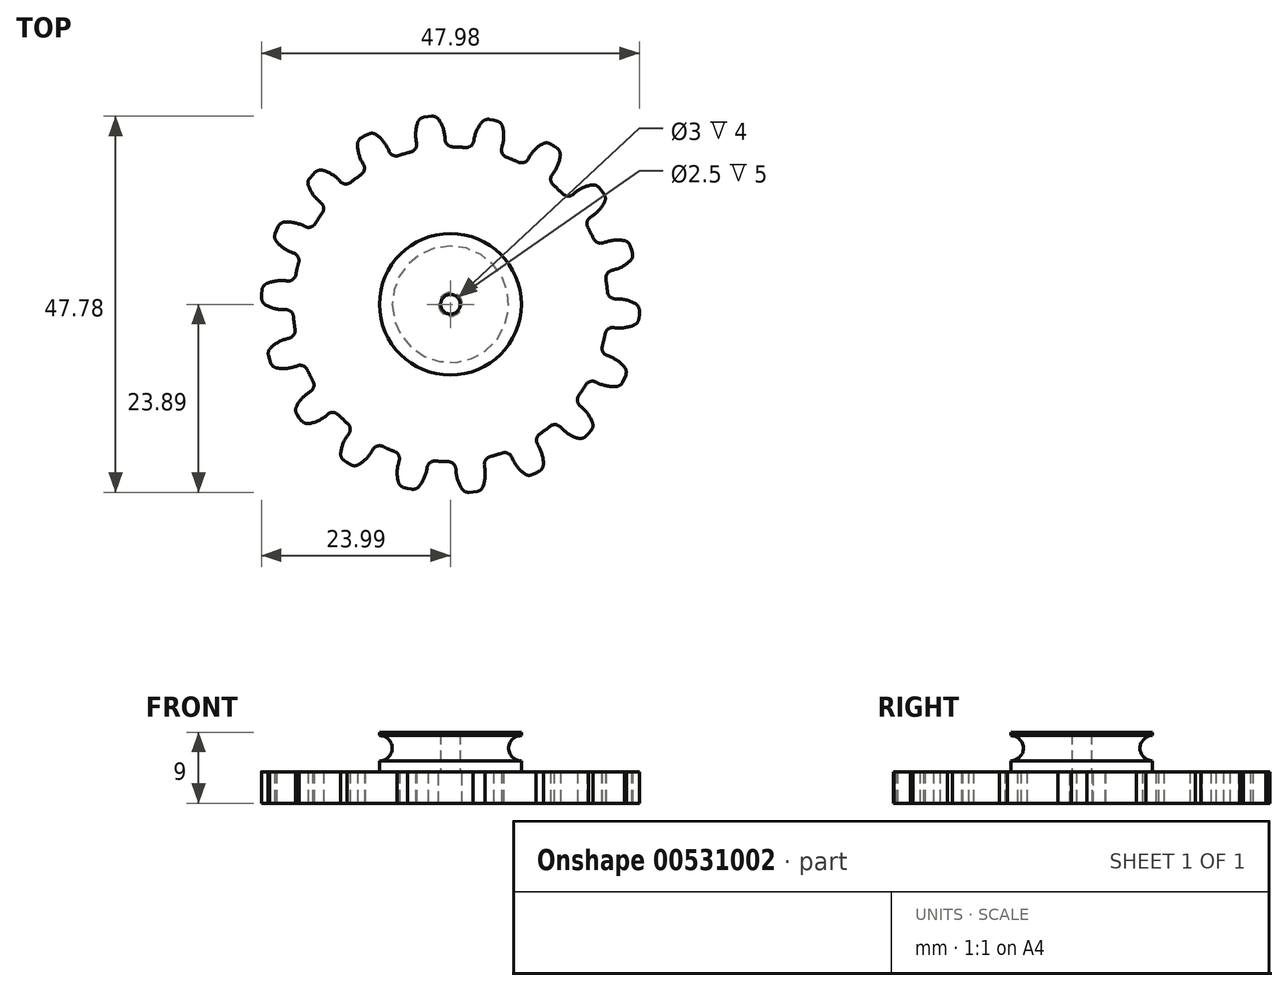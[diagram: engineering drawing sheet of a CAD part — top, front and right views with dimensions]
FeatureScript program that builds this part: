
annotation { "Feature Type Name" : "Feature", "Feature Type Description" : "" }
export const myFeature = defineFeature(function(context is Context, id is Id, definition is map)
    precondition{}
    {
        {
            var Q0;
            Q0=qCreatedBy(makeId("Top.planeOp"),FACE);
            var sketch = newSketch(context, id + "F0", { "sketchPlane" : qUnion([Q0])});
            skCircle(sketch, "E0", {"center": v(0, 0) * mm, "radius": 20 * mm, "construction": true});
            skLineSegment(sketch, "E1", {"start": v(0, 0) * mm, "end": v(29.94, 3.61) * mm, "construction": true});
            skLineSegment(sketch, "E2", {"start": v(0, 0) * mm, "end": v(27.72, -1.51) * mm, "construction": true});
            skLineSegment(sketch, "E3", {"start": v(0, 0) * mm, "end": v(20.99, 0.69) * mm, "construction": true});
            skLineSegment(sketch, "E4", {"start": v(0, 0) * mm, "end": v(24, -0.26) * mm, "construction": true});
            skArc(sketch, "E5", {"start": v(23.48, 0.07) * mm, "mid": v(22.28, 0.55) * mm, "end": v(20.99, 0.69) * mm});
            skArc(sketch, "E6", {"start": v(19.86, 2.4) * mm, "mid": v(19.9, 2) * mm, "end": v(19.94, 1.6) * mm});
            skLineSegment(sketch, "E7", {"start": v(20.96, 0.69) * mm, "end": v(20.99, 0.69) * mm});
            skLineSegment(sketch, "E8", {"start": v(24, -0.8) * mm, "end": v(23.99, -1.3) * mm});
            skLineSegment(sketch, "E9", {"start": v(0, 0) * mm, "end": v(19.86, 2.4) * mm});
            skLineSegment(sketch, "E10.MirrorCS", {"start": v(0, 0) * mm, "end": v(19.48, -4.54) * mm});
            skArc(sketch, "E11.MirrorCS", {"start": v(19.48, -4.54) * mm, "mid": v(19.56, -4.15) * mm, "end": v(19.64, -3.77) * mm});
            skLineSegment(sketch, "E12.MirrorCS", {"start": v(20.77, -2.96) * mm, "end": v(20.79, -2.97) * mm});
            skArc(sketch, "E13.MirrorCS", {"start": v(23.34, -2.63) * mm, "mid": v(22.09, -2.97) * mm, "end": v(20.79, -2.97) * mm});
            skLineSegment(sketch, "E14.MirrorCS", {"start": v(23.94, -1.8) * mm, "end": v(23.99, -1.3) * mm});
            skPoint(sketch, "E15.visualSharp", {"position": v(19.8, -2.83) * mm});
            skArc(sketch, "E15.filletArc", {"start": v(20.77, -2.96) * mm, "mid": v(20.04, -3.14) * mm, "end": v(19.64, -3.77) * mm});
            skPoint(sketch, "E16.visualSharp", {"position": v(19.99, 0.65) * mm});
            skArc(sketch, "E16.filletArc", {"start": v(19.94, 1.6) * mm, "mid": v(20.27, 0.94) * mm, "end": v(20.96, 0.69) * mm});
            skPoint(sketch, "E17.visualSharp", {"position": v(24, -0.26) * mm});
            skArc(sketch, "E17.filletArc", {"start": v(24, -0.8) * mm, "mid": v(23.86, -0.3) * mm, "end": v(23.48, 0.07) * mm});
            skPoint(sketch, "E18.visualSharp", {"position": v(23.88, -2.35) * mm});
            skArc(sketch, "E18.filletArc", {"start": v(23.34, -2.63) * mm, "mid": v(23.75, -2.3) * mm, "end": v(23.94, -1.8) * mm});
            skSolve(sketch);
        }
        {
            var Q0;
            Q0=qSketchRegion(id+"F0",true);
            extrude(context, id + "F1", {"entities" : qUnion([Q0]), "depth" : 4 * mm, "offsetDistance" : 25 * mm});
        }
        {
            var Q0;
            Q0=makeQuery(id+"F1.opExtrude","SWEPT_BODY",BODY,{"disambiguationData":[OSD([sQuery(id+"F0.wireOp",EDGE,"E5"),sQuery(id+"F0.wireOp",EDGE,"E6"),sQuery(id+"F0.wireOp",EDGE,"E7"),sQuery(id+"F0.wireOp",EDGE,"E8"),sQuery(id+"F0.wireOp",EDGE,"E9"),sQuery(id+"F0.wireOp",EDGE,"E10.MirrorCS"),sQuery(id+"F0.wireOp",EDGE,"E11.MirrorCS"),sQuery(id+"F0.wireOp",EDGE,"E12.MirrorCS"),sQuery(id+"F0.wireOp",EDGE,"E13.MirrorCS"),sQuery(id+"F0.wireOp",EDGE,"E14.MirrorCS"),sQuery(id+"F0.wireOp",EDGE,"E15.filletArc"),sQuery(id+"F0.wireOp",EDGE,"E16.filletArc"),sQuery(id+"F0.wireOp",EDGE,"E17.filletArc"),sQuery(id+"F0.wireOp",EDGE,"E18.filletArc")])]});
            var Q1;
            Q1=makeQuery(id+"F1.opExtrude","SWEPT_EDGE",EDGE,{"disambiguationData":[OSD([sQuery(id+"F0.wireOp",EDGE,"E9"),sQuery(id+"F0.wireOp",EDGE,"E10.MirrorCS")])]});
            circularPattern(context, id + "F2", {"entities" : qUnion([Q0]), "axis" : qUnion([Q1]), "angle" : 360 * degree, "instanceCount" : 18, "oppositeDirection" : true, "equalSpace" : true, "computeTransformsWithoutBuiltin" : true});
        }
        {
            var Q0;
            Q0=makeQuery(id+"F2.opPattern","COPY",BODY,{"derivedFrom":makeQuery(id+"F1.opExtrude","SWEPT_BODY",BODY,{"disambiguationData":[OSD([sQuery(id+"F0.wireOp",EDGE,"E5"),sQuery(id+"F0.wireOp",EDGE,"E6"),sQuery(id+"F0.wireOp",EDGE,"E7"),sQuery(id+"F0.wireOp",EDGE,"E8"),sQuery(id+"F0.wireOp",EDGE,"E9"),sQuery(id+"F0.wireOp",EDGE,"E10.MirrorCS"),sQuery(id+"F0.wireOp",EDGE,"E11.MirrorCS"),sQuery(id+"F0.wireOp",EDGE,"E12.MirrorCS"),sQuery(id+"F0.wireOp",EDGE,"E13.MirrorCS"),sQuery(id+"F0.wireOp",EDGE,"E14.MirrorCS"),sQuery(id+"F0.wireOp",EDGE,"E15.filletArc"),sQuery(id+"F0.wireOp",EDGE,"E16.filletArc"),sQuery(id+"F0.wireOp",EDGE,"E17.filletArc"),sQuery(id+"F0.wireOp",EDGE,"E18.filletArc")])]}),"instanceName":"6"});
            var Q1;
            Q1=makeQuery(id+"F2.opPattern","COPY",BODY,{"derivedFrom":makeQuery(id+"F1.opExtrude","SWEPT_BODY",BODY,{"disambiguationData":[OSD([sQuery(id+"F0.wireOp",EDGE,"E5"),sQuery(id+"F0.wireOp",EDGE,"E6"),sQuery(id+"F0.wireOp",EDGE,"E7"),sQuery(id+"F0.wireOp",EDGE,"E8"),sQuery(id+"F0.wireOp",EDGE,"E9"),sQuery(id+"F0.wireOp",EDGE,"E10.MirrorCS"),sQuery(id+"F0.wireOp",EDGE,"E11.MirrorCS"),sQuery(id+"F0.wireOp",EDGE,"E12.MirrorCS"),sQuery(id+"F0.wireOp",EDGE,"E13.MirrorCS"),sQuery(id+"F0.wireOp",EDGE,"E14.MirrorCS"),sQuery(id+"F0.wireOp",EDGE,"E15.filletArc"),sQuery(id+"F0.wireOp",EDGE,"E16.filletArc"),sQuery(id+"F0.wireOp",EDGE,"E17.filletArc"),sQuery(id+"F0.wireOp",EDGE,"E18.filletArc")])]}),"instanceName":"12"});
            var Q2;
            Q2=makeQuery(id+"F2.opPattern","COPY",BODY,{"derivedFrom":makeQuery(id+"F1.opExtrude","SWEPT_BODY",BODY,{"disambiguationData":[OSD([sQuery(id+"F0.wireOp",EDGE,"E5"),sQuery(id+"F0.wireOp",EDGE,"E6"),sQuery(id+"F0.wireOp",EDGE,"E7"),sQuery(id+"F0.wireOp",EDGE,"E8"),sQuery(id+"F0.wireOp",EDGE,"E9"),sQuery(id+"F0.wireOp",EDGE,"E10.MirrorCS"),sQuery(id+"F0.wireOp",EDGE,"E11.MirrorCS"),sQuery(id+"F0.wireOp",EDGE,"E12.MirrorCS"),sQuery(id+"F0.wireOp",EDGE,"E13.MirrorCS"),sQuery(id+"F0.wireOp",EDGE,"E14.MirrorCS"),sQuery(id+"F0.wireOp",EDGE,"E15.filletArc"),sQuery(id+"F0.wireOp",EDGE,"E16.filletArc"),sQuery(id+"F0.wireOp",EDGE,"E17.filletArc"),sQuery(id+"F0.wireOp",EDGE,"E18.filletArc")])]}),"instanceName":"14"});
            var Q3;
            Q3=makeQuery(id+"F2.opPattern","COPY",BODY,{"derivedFrom":makeQuery(id+"F1.opExtrude","SWEPT_BODY",BODY,{"disambiguationData":[OSD([sQuery(id+"F0.wireOp",EDGE,"E5"),sQuery(id+"F0.wireOp",EDGE,"E6"),sQuery(id+"F0.wireOp",EDGE,"E7"),sQuery(id+"F0.wireOp",EDGE,"E8"),sQuery(id+"F0.wireOp",EDGE,"E9"),sQuery(id+"F0.wireOp",EDGE,"E10.MirrorCS"),sQuery(id+"F0.wireOp",EDGE,"E11.MirrorCS"),sQuery(id+"F0.wireOp",EDGE,"E12.MirrorCS"),sQuery(id+"F0.wireOp",EDGE,"E13.MirrorCS"),sQuery(id+"F0.wireOp",EDGE,"E14.MirrorCS"),sQuery(id+"F0.wireOp",EDGE,"E15.filletArc"),sQuery(id+"F0.wireOp",EDGE,"E16.filletArc"),sQuery(id+"F0.wireOp",EDGE,"E17.filletArc"),sQuery(id+"F0.wireOp",EDGE,"E18.filletArc")])]}),"instanceName":"13"});
            var Q4;
            Q4=makeQuery(id+"F2.opPattern","COPY",BODY,{"derivedFrom":makeQuery(id+"F1.opExtrude","SWEPT_BODY",BODY,{"disambiguationData":[OSD([sQuery(id+"F0.wireOp",EDGE,"E5"),sQuery(id+"F0.wireOp",EDGE,"E6"),sQuery(id+"F0.wireOp",EDGE,"E7"),sQuery(id+"F0.wireOp",EDGE,"E8"),sQuery(id+"F0.wireOp",EDGE,"E9"),sQuery(id+"F0.wireOp",EDGE,"E10.MirrorCS"),sQuery(id+"F0.wireOp",EDGE,"E11.MirrorCS"),sQuery(id+"F0.wireOp",EDGE,"E12.MirrorCS"),sQuery(id+"F0.wireOp",EDGE,"E13.MirrorCS"),sQuery(id+"F0.wireOp",EDGE,"E14.MirrorCS"),sQuery(id+"F0.wireOp",EDGE,"E15.filletArc"),sQuery(id+"F0.wireOp",EDGE,"E16.filletArc"),sQuery(id+"F0.wireOp",EDGE,"E17.filletArc"),sQuery(id+"F0.wireOp",EDGE,"E18.filletArc")])]}),"instanceName":"9"});
            var Q5;
            Q5=makeQuery(id+"F2.opPattern","COPY",BODY,{"derivedFrom":makeQuery(id+"F1.opExtrude","SWEPT_BODY",BODY,{"disambiguationData":[OSD([sQuery(id+"F0.wireOp",EDGE,"E5"),sQuery(id+"F0.wireOp",EDGE,"E6"),sQuery(id+"F0.wireOp",EDGE,"E7"),sQuery(id+"F0.wireOp",EDGE,"E8"),sQuery(id+"F0.wireOp",EDGE,"E9"),sQuery(id+"F0.wireOp",EDGE,"E10.MirrorCS"),sQuery(id+"F0.wireOp",EDGE,"E11.MirrorCS"),sQuery(id+"F0.wireOp",EDGE,"E12.MirrorCS"),sQuery(id+"F0.wireOp",EDGE,"E13.MirrorCS"),sQuery(id+"F0.wireOp",EDGE,"E14.MirrorCS"),sQuery(id+"F0.wireOp",EDGE,"E15.filletArc"),sQuery(id+"F0.wireOp",EDGE,"E16.filletArc"),sQuery(id+"F0.wireOp",EDGE,"E17.filletArc"),sQuery(id+"F0.wireOp",EDGE,"E18.filletArc")])]}),"instanceName":"10"});
            var Q6;
            Q6=makeQuery(id+"F2.opPattern","COPY",BODY,{"derivedFrom":makeQuery(id+"F1.opExtrude","SWEPT_BODY",BODY,{"disambiguationData":[OSD([sQuery(id+"F0.wireOp",EDGE,"E5"),sQuery(id+"F0.wireOp",EDGE,"E6"),sQuery(id+"F0.wireOp",EDGE,"E7"),sQuery(id+"F0.wireOp",EDGE,"E8"),sQuery(id+"F0.wireOp",EDGE,"E9"),sQuery(id+"F0.wireOp",EDGE,"E10.MirrorCS"),sQuery(id+"F0.wireOp",EDGE,"E11.MirrorCS"),sQuery(id+"F0.wireOp",EDGE,"E12.MirrorCS"),sQuery(id+"F0.wireOp",EDGE,"E13.MirrorCS"),sQuery(id+"F0.wireOp",EDGE,"E14.MirrorCS"),sQuery(id+"F0.wireOp",EDGE,"E15.filletArc"),sQuery(id+"F0.wireOp",EDGE,"E16.filletArc"),sQuery(id+"F0.wireOp",EDGE,"E17.filletArc"),sQuery(id+"F0.wireOp",EDGE,"E18.filletArc")])]}),"instanceName":"11"});
            var Q7;
            Q7=makeQuery(id+"F2.opPattern","COPY",BODY,{"derivedFrom":makeQuery(id+"F1.opExtrude","SWEPT_BODY",BODY,{"disambiguationData":[OSD([sQuery(id+"F0.wireOp",EDGE,"E5"),sQuery(id+"F0.wireOp",EDGE,"E6"),sQuery(id+"F0.wireOp",EDGE,"E7"),sQuery(id+"F0.wireOp",EDGE,"E8"),sQuery(id+"F0.wireOp",EDGE,"E9"),sQuery(id+"F0.wireOp",EDGE,"E10.MirrorCS"),sQuery(id+"F0.wireOp",EDGE,"E11.MirrorCS"),sQuery(id+"F0.wireOp",EDGE,"E12.MirrorCS"),sQuery(id+"F0.wireOp",EDGE,"E13.MirrorCS"),sQuery(id+"F0.wireOp",EDGE,"E14.MirrorCS"),sQuery(id+"F0.wireOp",EDGE,"E15.filletArc"),sQuery(id+"F0.wireOp",EDGE,"E16.filletArc"),sQuery(id+"F0.wireOp",EDGE,"E17.filletArc"),sQuery(id+"F0.wireOp",EDGE,"E18.filletArc")])]}),"instanceName":"5"});
            var Q8;
            Q8=makeQuery(id+"F2.opPattern","COPY",BODY,{"derivedFrom":makeQuery(id+"F1.opExtrude","SWEPT_BODY",BODY,{"disambiguationData":[OSD([sQuery(id+"F0.wireOp",EDGE,"E5"),sQuery(id+"F0.wireOp",EDGE,"E6"),sQuery(id+"F0.wireOp",EDGE,"E7"),sQuery(id+"F0.wireOp",EDGE,"E8"),sQuery(id+"F0.wireOp",EDGE,"E9"),sQuery(id+"F0.wireOp",EDGE,"E10.MirrorCS"),sQuery(id+"F0.wireOp",EDGE,"E11.MirrorCS"),sQuery(id+"F0.wireOp",EDGE,"E12.MirrorCS"),sQuery(id+"F0.wireOp",EDGE,"E13.MirrorCS"),sQuery(id+"F0.wireOp",EDGE,"E14.MirrorCS"),sQuery(id+"F0.wireOp",EDGE,"E15.filletArc"),sQuery(id+"F0.wireOp",EDGE,"E16.filletArc"),sQuery(id+"F0.wireOp",EDGE,"E17.filletArc"),sQuery(id+"F0.wireOp",EDGE,"E18.filletArc")])]}),"instanceName":"16"});
            var Q9;
            Q9=makeQuery(id+"F2.opPattern","COPY",BODY,{"derivedFrom":makeQuery(id+"F1.opExtrude","SWEPT_BODY",BODY,{"disambiguationData":[OSD([sQuery(id+"F0.wireOp",EDGE,"E5"),sQuery(id+"F0.wireOp",EDGE,"E6"),sQuery(id+"F0.wireOp",EDGE,"E7"),sQuery(id+"F0.wireOp",EDGE,"E8"),sQuery(id+"F0.wireOp",EDGE,"E9"),sQuery(id+"F0.wireOp",EDGE,"E10.MirrorCS"),sQuery(id+"F0.wireOp",EDGE,"E11.MirrorCS"),sQuery(id+"F0.wireOp",EDGE,"E12.MirrorCS"),sQuery(id+"F0.wireOp",EDGE,"E13.MirrorCS"),sQuery(id+"F0.wireOp",EDGE,"E14.MirrorCS"),sQuery(id+"F0.wireOp",EDGE,"E15.filletArc"),sQuery(id+"F0.wireOp",EDGE,"E16.filletArc"),sQuery(id+"F0.wireOp",EDGE,"E17.filletArc"),sQuery(id+"F0.wireOp",EDGE,"E18.filletArc")])]}),"instanceName":"17"});
            var Q10;
            Q10=makeQuery(id+"F2.opPattern","COPY",BODY,{"derivedFrom":makeQuery(id+"F1.opExtrude","SWEPT_BODY",BODY,{"disambiguationData":[OSD([sQuery(id+"F0.wireOp",EDGE,"E5"),sQuery(id+"F0.wireOp",EDGE,"E6"),sQuery(id+"F0.wireOp",EDGE,"E7"),sQuery(id+"F0.wireOp",EDGE,"E8"),sQuery(id+"F0.wireOp",EDGE,"E9"),sQuery(id+"F0.wireOp",EDGE,"E10.MirrorCS"),sQuery(id+"F0.wireOp",EDGE,"E11.MirrorCS"),sQuery(id+"F0.wireOp",EDGE,"E12.MirrorCS"),sQuery(id+"F0.wireOp",EDGE,"E13.MirrorCS"),sQuery(id+"F0.wireOp",EDGE,"E14.MirrorCS"),sQuery(id+"F0.wireOp",EDGE,"E15.filletArc"),sQuery(id+"F0.wireOp",EDGE,"E16.filletArc"),sQuery(id+"F0.wireOp",EDGE,"E17.filletArc"),sQuery(id+"F0.wireOp",EDGE,"E18.filletArc")])]}),"instanceName":"15"});
            var Q11;
            Q11=makeQuery(id+"F2.opPattern","COPY",BODY,{"derivedFrom":makeQuery(id+"F1.opExtrude","SWEPT_BODY",BODY,{"disambiguationData":[OSD([sQuery(id+"F0.wireOp",EDGE,"E5"),sQuery(id+"F0.wireOp",EDGE,"E6"),sQuery(id+"F0.wireOp",EDGE,"E7"),sQuery(id+"F0.wireOp",EDGE,"E8"),sQuery(id+"F0.wireOp",EDGE,"E9"),sQuery(id+"F0.wireOp",EDGE,"E10.MirrorCS"),sQuery(id+"F0.wireOp",EDGE,"E11.MirrorCS"),sQuery(id+"F0.wireOp",EDGE,"E12.MirrorCS"),sQuery(id+"F0.wireOp",EDGE,"E13.MirrorCS"),sQuery(id+"F0.wireOp",EDGE,"E14.MirrorCS"),sQuery(id+"F0.wireOp",EDGE,"E15.filletArc"),sQuery(id+"F0.wireOp",EDGE,"E16.filletArc"),sQuery(id+"F0.wireOp",EDGE,"E17.filletArc"),sQuery(id+"F0.wireOp",EDGE,"E18.filletArc")])]}),"instanceName":"7"});
            var Q12;
            Q12=makeQuery(id+"F2.opPattern","COPY",BODY,{"derivedFrom":makeQuery(id+"F1.opExtrude","SWEPT_BODY",BODY,{"disambiguationData":[OSD([sQuery(id+"F0.wireOp",EDGE,"E5"),sQuery(id+"F0.wireOp",EDGE,"E6"),sQuery(id+"F0.wireOp",EDGE,"E7"),sQuery(id+"F0.wireOp",EDGE,"E8"),sQuery(id+"F0.wireOp",EDGE,"E9"),sQuery(id+"F0.wireOp",EDGE,"E10.MirrorCS"),sQuery(id+"F0.wireOp",EDGE,"E11.MirrorCS"),sQuery(id+"F0.wireOp",EDGE,"E12.MirrorCS"),sQuery(id+"F0.wireOp",EDGE,"E13.MirrorCS"),sQuery(id+"F0.wireOp",EDGE,"E14.MirrorCS"),sQuery(id+"F0.wireOp",EDGE,"E15.filletArc"),sQuery(id+"F0.wireOp",EDGE,"E16.filletArc"),sQuery(id+"F0.wireOp",EDGE,"E17.filletArc"),sQuery(id+"F0.wireOp",EDGE,"E18.filletArc")])]}),"instanceName":"8"});
            var Q13;
            Q13=makeQuery(id+"F2.opPattern","COPY",BODY,{"derivedFrom":makeQuery(id+"F1.opExtrude","SWEPT_BODY",BODY,{"disambiguationData":[OSD([sQuery(id+"F0.wireOp",EDGE,"E5"),sQuery(id+"F0.wireOp",EDGE,"E6"),sQuery(id+"F0.wireOp",EDGE,"E7"),sQuery(id+"F0.wireOp",EDGE,"E8"),sQuery(id+"F0.wireOp",EDGE,"E9"),sQuery(id+"F0.wireOp",EDGE,"E10.MirrorCS"),sQuery(id+"F0.wireOp",EDGE,"E11.MirrorCS"),sQuery(id+"F0.wireOp",EDGE,"E12.MirrorCS"),sQuery(id+"F0.wireOp",EDGE,"E13.MirrorCS"),sQuery(id+"F0.wireOp",EDGE,"E14.MirrorCS"),sQuery(id+"F0.wireOp",EDGE,"E15.filletArc"),sQuery(id+"F0.wireOp",EDGE,"E16.filletArc"),sQuery(id+"F0.wireOp",EDGE,"E17.filletArc"),sQuery(id+"F0.wireOp",EDGE,"E18.filletArc")])]}),"instanceName":"2"});
            var Q14;
            Q14=makeQuery(id+"F2.opPattern","COPY",BODY,{"derivedFrom":makeQuery(id+"F1.opExtrude","SWEPT_BODY",BODY,{"disambiguationData":[OSD([sQuery(id+"F0.wireOp",EDGE,"E5"),sQuery(id+"F0.wireOp",EDGE,"E6"),sQuery(id+"F0.wireOp",EDGE,"E7"),sQuery(id+"F0.wireOp",EDGE,"E8"),sQuery(id+"F0.wireOp",EDGE,"E9"),sQuery(id+"F0.wireOp",EDGE,"E10.MirrorCS"),sQuery(id+"F0.wireOp",EDGE,"E11.MirrorCS"),sQuery(id+"F0.wireOp",EDGE,"E12.MirrorCS"),sQuery(id+"F0.wireOp",EDGE,"E13.MirrorCS"),sQuery(id+"F0.wireOp",EDGE,"E14.MirrorCS"),sQuery(id+"F0.wireOp",EDGE,"E15.filletArc"),sQuery(id+"F0.wireOp",EDGE,"E16.filletArc"),sQuery(id+"F0.wireOp",EDGE,"E17.filletArc"),sQuery(id+"F0.wireOp",EDGE,"E18.filletArc")])]}),"instanceName":"3"});
            var Q15;
            Q15=makeQuery(id+"F2.opPattern","COPY",BODY,{"derivedFrom":makeQuery(id+"F1.opExtrude","SWEPT_BODY",BODY,{"disambiguationData":[OSD([sQuery(id+"F0.wireOp",EDGE,"E5"),sQuery(id+"F0.wireOp",EDGE,"E6"),sQuery(id+"F0.wireOp",EDGE,"E7"),sQuery(id+"F0.wireOp",EDGE,"E8"),sQuery(id+"F0.wireOp",EDGE,"E9"),sQuery(id+"F0.wireOp",EDGE,"E10.MirrorCS"),sQuery(id+"F0.wireOp",EDGE,"E11.MirrorCS"),sQuery(id+"F0.wireOp",EDGE,"E12.MirrorCS"),sQuery(id+"F0.wireOp",EDGE,"E13.MirrorCS"),sQuery(id+"F0.wireOp",EDGE,"E14.MirrorCS"),sQuery(id+"F0.wireOp",EDGE,"E15.filletArc"),sQuery(id+"F0.wireOp",EDGE,"E16.filletArc"),sQuery(id+"F0.wireOp",EDGE,"E17.filletArc"),sQuery(id+"F0.wireOp",EDGE,"E18.filletArc")])]}),"instanceName":"4"});
            var Q16;
            Q16=makeQuery(id+"F2.opPattern","COPY",BODY,{"derivedFrom":makeQuery(id+"F1.opExtrude","SWEPT_BODY",BODY,{"disambiguationData":[OSD([sQuery(id+"F0.wireOp",EDGE,"E5"),sQuery(id+"F0.wireOp",EDGE,"E6"),sQuery(id+"F0.wireOp",EDGE,"E7"),sQuery(id+"F0.wireOp",EDGE,"E8"),sQuery(id+"F0.wireOp",EDGE,"E9"),sQuery(id+"F0.wireOp",EDGE,"E10.MirrorCS"),sQuery(id+"F0.wireOp",EDGE,"E11.MirrorCS"),sQuery(id+"F0.wireOp",EDGE,"E12.MirrorCS"),sQuery(id+"F0.wireOp",EDGE,"E13.MirrorCS"),sQuery(id+"F0.wireOp",EDGE,"E14.MirrorCS"),sQuery(id+"F0.wireOp",EDGE,"E15.filletArc"),sQuery(id+"F0.wireOp",EDGE,"E16.filletArc"),sQuery(id+"F0.wireOp",EDGE,"E17.filletArc"),sQuery(id+"F0.wireOp",EDGE,"E18.filletArc")])]}),"instanceName":"1"});
            var Q17;
            Q17=makeQuery(id+"F1.opExtrude","SWEPT_BODY",BODY,{"disambiguationData":[OSD([sQuery(id+"F0.wireOp",EDGE,"E5"),sQuery(id+"F0.wireOp",EDGE,"E6"),sQuery(id+"F0.wireOp",EDGE,"E7"),sQuery(id+"F0.wireOp",EDGE,"E8"),sQuery(id+"F0.wireOp",EDGE,"E9"),sQuery(id+"F0.wireOp",EDGE,"E10.MirrorCS"),sQuery(id+"F0.wireOp",EDGE,"E11.MirrorCS"),sQuery(id+"F0.wireOp",EDGE,"E12.MirrorCS"),sQuery(id+"F0.wireOp",EDGE,"E13.MirrorCS"),sQuery(id+"F0.wireOp",EDGE,"E14.MirrorCS"),sQuery(id+"F0.wireOp",EDGE,"E15.filletArc"),sQuery(id+"F0.wireOp",EDGE,"E16.filletArc"),sQuery(id+"F0.wireOp",EDGE,"E17.filletArc"),sQuery(id+"F0.wireOp",EDGE,"E18.filletArc")])]});
            booleanBodies(context, id + "F3", {"operationType" : BooleanOperationType.UNION, "tools" : qUnion([Q0, Q1, Q2, Q3, Q4, Q5, Q6, Q7, Q8, Q9, Q10, Q11, Q12, Q13, Q14, Q15, Q16, Q17])});
        }
        {
            var Q0;
            {var subQ0=makeQuery(id+"F1.opExtrude","CAP_FACE",FACE,{"disambiguationData":[OSD([sQuery(id+"F0.wireOp",EDGE,"E5"),sQuery(id+"F0.wireOp",EDGE,"E6"),sQuery(id+"F0.wireOp",EDGE,"E7"),sQuery(id+"F0.wireOp",EDGE,"E8"),sQuery(id+"F0.wireOp",EDGE,"E9"),sQuery(id+"F0.wireOp",EDGE,"E10.MirrorCS"),sQuery(id+"F0.wireOp",EDGE,"E11.MirrorCS"),sQuery(id+"F0.wireOp",EDGE,"E12.MirrorCS"),sQuery(id+"F0.wireOp",EDGE,"E13.MirrorCS"),sQuery(id+"F0.wireOp",EDGE,"E14.MirrorCS"),sQuery(id+"F0.wireOp",EDGE,"E15.filletArc"),sQuery(id+"F0.wireOp",EDGE,"E16.filletArc"),sQuery(id+"F0.wireOp",EDGE,"E17.filletArc"),sQuery(id+"F0.wireOp",EDGE,"E18.filletArc")])],"isStart":false});Q0=makeQuery(id+"F3.opBoolean","MERGE",FACE,{"derivedFrom":[subQ0,makeQuery(id+"F2.opPattern","COPY",FACE,{"derivedFrom":subQ0,"instanceName":"1"}),makeQuery(id+"F2.opPattern","COPY",FACE,{"derivedFrom":subQ0,"instanceName":"2"}),makeQuery(id+"F2.opPattern","COPY",FACE,{"derivedFrom":subQ0,"instanceName":"3"}),makeQuery(id+"F2.opPattern","COPY",FACE,{"derivedFrom":subQ0,"instanceName":"4"}),makeQuery(id+"F2.opPattern","COPY",FACE,{"derivedFrom":subQ0,"instanceName":"5"}),makeQuery(id+"F2.opPattern","COPY",FACE,{"derivedFrom":subQ0,"instanceName":"6"}),makeQuery(id+"F2.opPattern","COPY",FACE,{"derivedFrom":subQ0,"instanceName":"7"}),makeQuery(id+"F2.opPattern","COPY",FACE,{"derivedFrom":subQ0,"instanceName":"8"}),makeQuery(id+"F2.opPattern","COPY",FACE,{"derivedFrom":subQ0,"instanceName":"9"}),makeQuery(id+"F2.opPattern","COPY",FACE,{"derivedFrom":subQ0,"instanceName":"10"}),makeQuery(id+"F2.opPattern","COPY",FACE,{"derivedFrom":subQ0,"instanceName":"11"}),makeQuery(id+"F2.opPattern","COPY",FACE,{"derivedFrom":subQ0,"instanceName":"12"}),makeQuery(id+"F2.opPattern","COPY",FACE,{"derivedFrom":subQ0,"instanceName":"13"}),makeQuery(id+"F2.opPattern","COPY",FACE,{"derivedFrom":subQ0,"instanceName":"14"}),makeQuery(id+"F2.opPattern","COPY",FACE,{"derivedFrom":subQ0,"instanceName":"15"}),makeQuery(id+"F2.opPattern","COPY",FACE,{"derivedFrom":subQ0,"instanceName":"16"}),makeQuery(id+"F2.opPattern","COPY",FACE,{"derivedFrom":subQ0,"instanceName":"17"})]});}
            var sketch = newSketch(context, id + "F4", { "sketchPlane" : qUnion([Q0])});
            skCircle(sketch, "E19", {"center": v(0, 0) * mm, "radius": 1.5 * mm});
            skSolve(sketch);
        }
        {
            var Q0;
            Q0=qSketchRegion(id+"F4",true);
            var Q1;
            {var subQ0=makeQuery(id+"F1.opExtrude","CAP_FACE",FACE,{"disambiguationData":[OSD([sQuery(id+"F0.wireOp",EDGE,"E5"),sQuery(id+"F0.wireOp",EDGE,"E6"),sQuery(id+"F0.wireOp",EDGE,"E7"),sQuery(id+"F0.wireOp",EDGE,"E8"),sQuery(id+"F0.wireOp",EDGE,"E9"),sQuery(id+"F0.wireOp",EDGE,"E10.MirrorCS"),sQuery(id+"F0.wireOp",EDGE,"E11.MirrorCS"),sQuery(id+"F0.wireOp",EDGE,"E12.MirrorCS"),sQuery(id+"F0.wireOp",EDGE,"E13.MirrorCS"),sQuery(id+"F0.wireOp",EDGE,"E14.MirrorCS"),sQuery(id+"F0.wireOp",EDGE,"E15.filletArc"),sQuery(id+"F0.wireOp",EDGE,"E16.filletArc"),sQuery(id+"F0.wireOp",EDGE,"E17.filletArc"),sQuery(id+"F0.wireOp",EDGE,"E18.filletArc")])],"isStart":true});Q1=makeQuery(id+"F3.opBoolean","MERGE",FACE,{"derivedFrom":[subQ0,makeQuery(id+"F2.opPattern","COPY",FACE,{"derivedFrom":subQ0,"instanceName":"1"}),makeQuery(id+"F2.opPattern","COPY",FACE,{"derivedFrom":subQ0,"instanceName":"2"}),makeQuery(id+"F2.opPattern","COPY",FACE,{"derivedFrom":subQ0,"instanceName":"3"}),makeQuery(id+"F2.opPattern","COPY",FACE,{"derivedFrom":subQ0,"instanceName":"4"}),makeQuery(id+"F2.opPattern","COPY",FACE,{"derivedFrom":subQ0,"instanceName":"5"}),makeQuery(id+"F2.opPattern","COPY",FACE,{"derivedFrom":subQ0,"instanceName":"6"}),makeQuery(id+"F2.opPattern","COPY",FACE,{"derivedFrom":subQ0,"instanceName":"7"}),makeQuery(id+"F2.opPattern","COPY",FACE,{"derivedFrom":subQ0,"instanceName":"8"}),makeQuery(id+"F2.opPattern","COPY",FACE,{"derivedFrom":subQ0,"instanceName":"9"}),makeQuery(id+"F2.opPattern","COPY",FACE,{"derivedFrom":subQ0,"instanceName":"10"}),makeQuery(id+"F2.opPattern","COPY",FACE,{"derivedFrom":subQ0,"instanceName":"11"}),makeQuery(id+"F2.opPattern","COPY",FACE,{"derivedFrom":subQ0,"instanceName":"12"}),makeQuery(id+"F2.opPattern","COPY",FACE,{"derivedFrom":subQ0,"instanceName":"13"}),makeQuery(id+"F2.opPattern","COPY",FACE,{"derivedFrom":subQ0,"instanceName":"14"}),makeQuery(id+"F2.opPattern","COPY",FACE,{"derivedFrom":subQ0,"instanceName":"15"}),makeQuery(id+"F2.opPattern","COPY",FACE,{"derivedFrom":subQ0,"instanceName":"16"}),makeQuery(id+"F2.opPattern","COPY",FACE,{"derivedFrom":subQ0,"instanceName":"17"})]});}
            extrude(context, id + "F5", {"entities" : qUnion([Q0]), "operationType" : NewBodyOperationType.REMOVE, "endBound" : BoundingType.UP_TO_SURFACE, "oppositeDirection" : true, "depth" : 25 * mm, "endBoundEntityFace" : qUnion([Q1]), "offsetDistance" : 25 * mm});
        }
        {
            var Q0;
            Q0=makeQuery(id+"F2.opPattern","COPY",BODY,{"derivedFrom":makeQuery(id+"F1.opExtrude","SWEPT_BODY",BODY,{"disambiguationData":[OSD([sQuery(id+"F0.wireOp",EDGE,"E5"),sQuery(id+"F0.wireOp",EDGE,"E6"),sQuery(id+"F0.wireOp",EDGE,"E7"),sQuery(id+"F0.wireOp",EDGE,"E8"),sQuery(id+"F0.wireOp",EDGE,"E9"),sQuery(id+"F0.wireOp",EDGE,"E10.MirrorCS"),sQuery(id+"F0.wireOp",EDGE,"E11.MirrorCS"),sQuery(id+"F0.wireOp",EDGE,"E12.MirrorCS"),sQuery(id+"F0.wireOp",EDGE,"E13.MirrorCS"),sQuery(id+"F0.wireOp",EDGE,"E14.MirrorCS"),sQuery(id+"F0.wireOp",EDGE,"E15.filletArc"),sQuery(id+"F0.wireOp",EDGE,"E16.filletArc"),sQuery(id+"F0.wireOp",EDGE,"E17.filletArc"),sQuery(id+"F0.wireOp",EDGE,"E18.filletArc")])]}),"instanceName":"6"});
            transform(context, id + "F6", {"entities" : qUnion([Q0]), "transformType" : TransformType.TRANSLATION_3D, "dx" : 0 * mm, "dy" : 0 * mm, "dz" : 0 * mm, "makeCopy" : true});
        }
        {
            var Q0;
            Q0=makeQuery(id+"F6.opPattern","COPY",BODY,{"derivedFrom":makeQuery(id+"F2.opPattern","COPY",BODY,{"derivedFrom":makeQuery(id+"F1.opExtrude","SWEPT_BODY",BODY,{"disambiguationData":[OSD([sQuery(id+"F0.wireOp",EDGE,"E5"),sQuery(id+"F0.wireOp",EDGE,"E6"),sQuery(id+"F0.wireOp",EDGE,"E7"),sQuery(id+"F0.wireOp",EDGE,"E8"),sQuery(id+"F0.wireOp",EDGE,"E9"),sQuery(id+"F0.wireOp",EDGE,"E10.MirrorCS"),sQuery(id+"F0.wireOp",EDGE,"E11.MirrorCS"),sQuery(id+"F0.wireOp",EDGE,"E12.MirrorCS"),sQuery(id+"F0.wireOp",EDGE,"E13.MirrorCS"),sQuery(id+"F0.wireOp",EDGE,"E14.MirrorCS"),sQuery(id+"F0.wireOp",EDGE,"E15.filletArc"),sQuery(id+"F0.wireOp",EDGE,"E16.filletArc"),sQuery(id+"F0.wireOp",EDGE,"E17.filletArc"),sQuery(id+"F0.wireOp",EDGE,"E18.filletArc")])]}),"instanceName":"6"}),"instanceName":"1"});
            deleteBodies(context, id + "F7", {"entities" : qUnion([Q0])});
        }
        {
            var Q0;
            Q0=qCreatedBy(makeId("Right.planeOp"),FACE);
            var sketch = newSketch(context, id + "F8", { "sketchPlane" : qUnion([Q0])});
            skLineSegment(sketch, "E20", {"start": v(0, 4) * mm, "end": v(1.25, 4) * mm, "construction": true});
            skLineSegment(sketch, "E21", {"start": v(1.25, 4) * mm, "end": v(9, 4) * mm});
            skLineSegment(sketch, "E22", {"start": v(9, 4) * mm, "end": v(9, 5.4) * mm});
            skLineSegment(sketch, "E23", {"start": v(9, 8.6) * mm, "end": v(9, 9) * mm});
            skLineSegment(sketch, "E24", {"start": v(9, 5.4) * mm, "end": v(9, 7) * mm, "construction": true});
            skLineSegment(sketch, "E25", {"start": v(9, 7) * mm, "end": v(9, 8.6) * mm, "construction": true});
            skLineSegment(sketch, "E26", {"start": v(9, 7) * mm, "end": v(7.4, 7) * mm, "construction": true});
            skArc(sketch, "E27", {"start": v(9, 8.6) * mm, "mid": v(7.4, 7) * mm, "end": v(9, 5.4) * mm});
            skLineSegment(sketch, "E28", {"start": v(9, 9) * mm, "end": v(1.25, 9) * mm});
            skLineSegment(sketch, "E29", {"start": v(1.25, 9) * mm, "end": v(1.25, 4) * mm});
            skLineSegment(sketch, "E30", {"start": v(0, 4) * mm, "end": v(0, 9) * mm, "construction": true});
            skSolve(sketch);
        }
        {
            var Q0;
            Q0=makeQuery(id+"F8.imprint","IMPRINT",FACE,{"disambiguationData":[TD([[makeQuery(id+"F8.imprint","IMPRINT",EDGE,{"derivedFrom":sQuery(id+"F8.wireOp",EDGE,"E21")}),1.0]])]});
            var Q1;
            Q1=sQuery(id+"F8.wireOp",EDGE,"E30");
            revolve(context, id + "F9", {"operationType" : NewBodyOperationType.ADD, "entities" : qUnion([Q0]), "axis" : qUnion([Q1]), "revolveType" : RevolveType.FULL});
        }
    });
